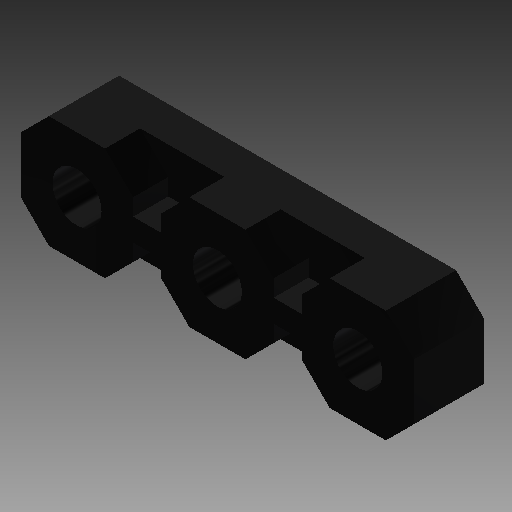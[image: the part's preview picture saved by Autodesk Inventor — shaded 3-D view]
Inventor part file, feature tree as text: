
AUTODESK INVENTOR PART (.ipt)
format: ipt  version: 2018 (Build 220112000, 112)  size: 268,288 bytes
history: native  units: mm (DEFAULTED — no unit token found)
features: extrude x7, sketch x6, other x3, chamfer x1, hole x1, pattern_linear x1
ambient origin geometry x8: Origin, YZ Plane, XZ Plane, XY Plane, X Axis, Y Axis, Z Axis, Center Point
bodies: Solid1 (feature_tree)
feature tree (19):
  extrude  "Extrusion1"  Depth=35.56mm
  chamfer  "Chamfer1"  Distance=3.175mm
  extrude  "Extrusion2"  Depth=10.16mm
  extrude  "Extrusion3"  Depth=2.54mm
  hole  "Hole1"  [1 undecoded]
  extrude  "Extrusion4"  Depth=2.54mm
  pattern_linear  "Rectangular Pattern1"  Spacing1=2.54mm  [1 undecoded]
  sketch  "Sketch1"  dims[d0=10.16mm d1=35.56mm d2=3.175mm d3=0.0mm]
  sketch  "Sketch2"  dims[d4=2.54mm d5=3.175mm d6=45.0deg d7=10.16mm]
  sketch  "Sketch3"  dims[d8=2.54mm d9=2.54mm]
  sketch  "Sketch4"  dims[d10=10.16mm d11=2.54mm]
  sketch  "Sketch5"  dims[d12=2.54mm d13=2.54mm]
  sketch  "Sketch6"  dims[d14=2.54mm d15=2.54mm d16=10.16mm d17=2.54mm d18=2.54mm d19=2.032mm d20=4.064mm d21=3.175mm d22=0.0mm d23=5.08mm d24=5.08mm d25=5.08mm d26=5.08mm d27=5.08mm d28=5.08mm d29=4.191mm d30=4.191mm d31=4.191mm d32=4.191mm d33=2.0955mm d34=2.0955mm d35=2.0955mm d36=2.0955mm d37=6.985mm d38=0.0mm d39=5.08mm d40=5.08mm d41=12.7mm d42=12.7mm d43=5.08mm d44=5.08mm d45=4.445mm d46=12.7mm d47=9.525mm d48=6.35mm d49=14.3117mm d50=19.05mm d51=20.594885mm d52=7.62mm d53=7.62mm d54=7.62mm d55=6.35mm d56=1.524mm d57=1.524mm d58=1.905mm d59=0.0mm d60=25.4mm d61=0.0mm d62=30.0mm d64=12.7mm d65=0.0mm d66=0.0mm d67=0.0mm d68=0.0mm d69=0.0mm d70=0.0mm]
  other  "Srf1"
  other  "Srf2"
  other  "Srf3"
  extrude  "ExtrusionSrf1"  Depth=10.16mm
  extrude  "ExtrusionSrf2"  Depth=2.54mm
  extrude  "ExtrusionSrf3"  Depth=2.54mm
note: 2 required parameter values undecoded (feature->parameter linkage not recoverable at this tier; creation-order binding heuristic only, values carry confidence <= 0.55)
